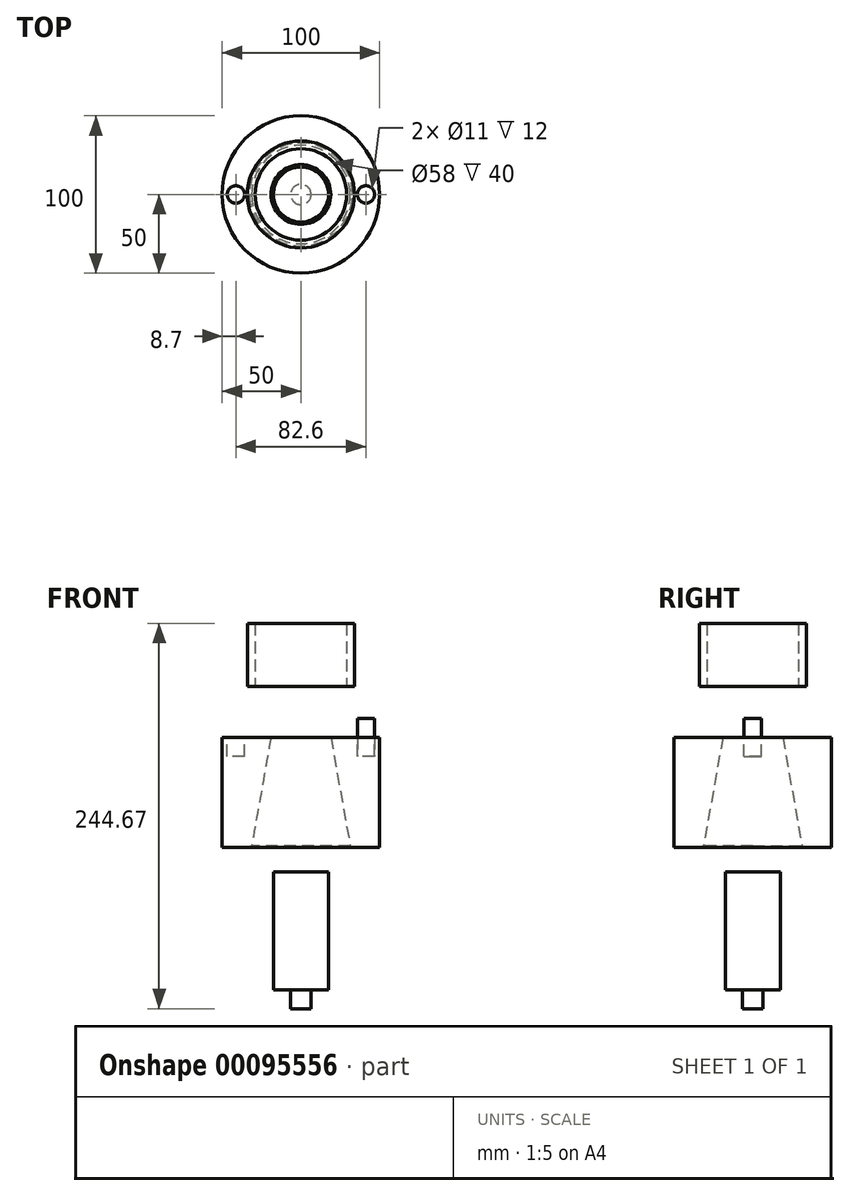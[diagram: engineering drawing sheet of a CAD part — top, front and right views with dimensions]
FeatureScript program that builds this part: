
annotation { "Feature Type Name" : "Feature", "Feature Type Description" : "" }
export const myFeature = defineFeature(function(context is Context, id is Id, definition is map)
    precondition{}
    {
        {
            var Q0;
            Q0=qCreatedBy(makeId("Front.planeOp"),FACE);
            var sketch = newSketch(context, id + "F0", { "sketchPlane" : qUnion([Q0])});
            skLineSegment(sketch, "E0.bottom", {"start": v(50, 35) * mm, "end": v(-50, 35) * mm});
            skLineSegment(sketch, "E0.top", {"start": v(50, -35) * mm, "end": v(-50, -35) * mm});
            skLineSegment(sketch, "E0.left", {"start": v(50, 35) * mm, "end": v(50, -35) * mm});
            skLineSegment(sketch, "E0.right", {"start": v(-50, 35) * mm, "end": v(-50, -35) * mm});
            skPoint(sketch, "E0.middle", {"position": v(0, 0) * mm});
            skLineSegment(sketch, "E1", {"start": v(-19, 35) * mm, "end": v(-31.5, -35) * mm});
            skLineSegment(sketch, "E2.MirrorCS", {"start": v(19, 35) * mm, "end": v(31.5, -35) * mm});
            skLineSegment(sketch, "E3.bottom", {"start": v(34, 107.38) * mm, "end": v(-34, 107.38) * mm});
            skLineSegment(sketch, "E3.top", {"start": v(34, 67.38) * mm, "end": v(-34, 67.38) * mm});
            skLineSegment(sketch, "E3.left", {"start": v(34, 107.38) * mm, "end": v(34, 67.38) * mm});
            skLineSegment(sketch, "E3.right", {"start": v(-34, 107.38) * mm, "end": v(-34, 67.38) * mm});
            skPoint(sketch, "E3.middle", {"position": v(0, 87.38) * mm});
            skLineSegment(sketch, "E4.bottom", {"start": v(29, 107.38) * mm, "end": v(-29, 107.38) * mm});
            skLineSegment(sketch, "E4.top", {"start": v(29, 67.38) * mm, "end": v(-29, 67.38) * mm});
            skLineSegment(sketch, "E4.left", {"start": v(29, 107.38) * mm, "end": v(29, 67.38) * mm});
            skLineSegment(sketch, "E4.right", {"start": v(-29, 107.38) * mm, "end": v(-29, 67.38) * mm});
            skLineSegment(sketch, "E5.bottom", {"start": v(17.5, -125.29) * mm, "end": v(-17.5, -125.29) * mm});
            skLineSegment(sketch, "E5.top", {"start": v(17.5, -50.29) * mm, "end": v(-17.5, -50.29) * mm});
            skLineSegment(sketch, "E5.left", {"start": v(17.5, -125.29) * mm, "end": v(17.5, -50.29) * mm});
            skLineSegment(sketch, "E5.right", {"start": v(-17.5, -125.29) * mm, "end": v(-17.5, -50.29) * mm});
            skPoint(sketch, "E5.middle", {"position": v(0, -87.79) * mm});
            skLineSegment(sketch, "E6.bottom", {"start": v(-6.5, -137.29) * mm, "end": v(6.5, -137.29) * mm});
            skLineSegment(sketch, "E6.left", {"start": v(-6.5, -137.29) * mm, "end": v(-6.5, -125.29) * mm});
            skLineSegment(sketch, "E6.right", {"start": v(6.5, -137.29) * mm, "end": v(6.5, -125.29) * mm});
            skPoint(sketch, "E6.middle", {"position": v(0, -125.29) * mm});
            skPoint(sketch, "E7", {"position": v(-6.5, -125.29) * mm});
            skPoint(sketch, "E8", {"position": v(6.5, -125.29) * mm});
            skLineSegment(sketch, "E9", {"start": v(0, -170.14) * mm, "end": v(0, 147.54) * mm});
            skPoint(sketch, "E9.endSnap0", {"position": v(0, 107.38) * mm});
            skPoint(sketch, "E10.middle", {"position": v(0, 35) * mm});
            skPoint(sketch, "E11", {"position": v(-41.3, 35) * mm});
            skPoint(sketch, "E12", {"position": v(41.3, 35) * mm});
            skLineSegment(sketch, "E13.bottom", {"start": v(-35.8, 47) * mm, "end": v(-46.8, 47) * mm});
            skLineSegment(sketch, "E13.top", {"start": v(-35.8, 23) * mm, "end": v(-46.8, 23) * mm});
            skLineSegment(sketch, "E13.left", {"start": v(-35.8, 47) * mm, "end": v(-35.8, 23) * mm});
            skLineSegment(sketch, "E13.right", {"start": v(-46.8, 47) * mm, "end": v(-46.8, 23) * mm});
            skLineSegment(sketch, "E14.MirrorCS", {"start": v(35.8, 23) * mm, "end": v(46.8, 23) * mm});
            skLineSegment(sketch, "E15.MirrorCS", {"start": v(35.8, 47) * mm, "end": v(35.8, 23) * mm});
            skLineSegment(sketch, "E16.MirrorCS", {"start": v(46.8, 47) * mm, "end": v(46.8, 23) * mm});
            skLineSegment(sketch, "E17.MirrorCS", {"start": v(35.8, 47) * mm, "end": v(46.8, 47) * mm});
            skLineSegment(sketch, "E18", {"start": v(-41.3, 23) * mm, "end": v(-41.3, 57) * mm});
            skLineSegment(sketch, "E19", {"start": v(41.3, 23) * mm, "end": v(41.3, 51.68) * mm});
            skPoint(sketch, "E19.endSnap0", {"position": v(41.3, 47) * mm});
            skSolve(sketch);
        }
        {
            var Q0;
            {var subQ0=sQuery(id+"F0.wireOp",EDGE,"E3.right");Q0=makeQuery(id+"F0.imprint","IMPRINT",FACE,{"disambiguationData":[TD([[makeQuery(id+"F0.imprint","IMPRINT",EDGE,{"derivedFrom":subQ0}),1.0]])]});}
            var Q1;
            Q1=sQuery(id+"F0.wireOp",EDGE,"E9");
            revolve(context, id + "F1", {"entities" : qUnion([Q0]), "axis" : qUnion([Q1]), "revolveType" : RevolveType.FULL});
        }
        {
            var Q0;
            {var subQ0=sQuery(id+"F0.wireOp",EDGE,"E0.right");Q0=makeQuery(id+"F0.imprint","IMPRINT",FACE,{"disambiguationData":[TD([[makeQuery(id+"F0.imprint","IMPRINT",EDGE,{"derivedFrom":subQ0}),1.0]])]});}
            var Q1;
            {var subQ5=sQuery(id+"F0.wireOp",EDGE,"E13.top");Q1=makeQuery(id+"F0.imprint","IMPRINT",FACE,{"disambiguationData":[TD([[makeQuery(id+"F0.imprint","IMPRINT",EDGE,{"derivedFrom":subQ5}),-1.0]])]});}
            var Q2;
            Q2=sQuery(id+"F0.wireOp",EDGE,"E9");
            revolve(context, id + "F2", {"entities" : qUnion([Q0, Q1]), "axis" : qUnion([Q2]), "revolveType" : RevolveType.FULL});
        }
        {
            var Q0;
            {var subQ0=sQuery(id+"F0.wireOp",EDGE,"E5.right");Q0=makeQuery(id+"F0.imprint","IMPRINT",FACE,{"disambiguationData":[TD([[makeQuery(id+"F0.imprint","IMPRINT",EDGE,{"derivedFrom":subQ0}),-1.0]])]});}
            var Q1;
            {var subQ0=sQuery(id+"F0.wireOp",EDGE,"E6.left");Q1=makeQuery(id+"F0.imprint","IMPRINT",FACE,{"disambiguationData":[TD([[makeQuery(id+"F0.imprint","IMPRINT",EDGE,{"derivedFrom":subQ0}),-1.0]])]});}
            var Q2;
            Q2=sQuery(id+"F0.wireOp",EDGE,"E9");
            revolve(context, id + "F3", {"entities" : qUnion([Q0, Q1]), "axis" : qUnion([Q2]), "revolveType" : RevolveType.FULL});
        }
        {
            var Q0;
            Q0=makeQuery(id+"F2.opRevolve","SWEPT_EDGE",EDGE,{"disambiguationData":[OSD([sQuery(id+"F0.wireOp",EDGE,"E0.top"),sQuery(id+"F0.wireOp",EDGE,"E1")])]});
            chamfer(context, id + "F4", {"entities" : qUnion([Q0]), "width" : 1.5 * mm});
        }
        {
            var Q0;
            {var subQ0=sQuery(id+"F0.wireOp",EDGE,"E13.right");var subQ1=sQuery(id+"F0.wireOp",EDGE,"E0.bottom");var subQ2=makeQuery(id+"F0.imprint","INTERSECT",VERTEX,{"derivedFrom":[subQ1,subQ0]});Q0=makeQuery(id+"F0.imprint","IMPRINT",FACE,{"disambiguationData":[TD([[makeQuery(id+"F0.imprint","IMPRINT",EDGE,{"disambiguationData":[TD([[subQ2,1.0]])],"derivedFrom":subQ1}),1.0]])]});}
            var Q1;
            {var subQ0=sQuery(id+"F0.wireOp",EDGE,"E13.right");var subQ1=sQuery(id+"F0.wireOp",EDGE,"E0.bottom");var subQ2=makeQuery(id+"F0.imprint","INTERSECT",VERTEX,{"derivedFrom":[subQ1,subQ0]});Q1=makeQuery(id+"F0.imprint","IMPRINT",FACE,{"disambiguationData":[TD([[makeQuery(id+"F0.imprint","IMPRINT",EDGE,{"disambiguationData":[TD([[subQ2,1.0]])],"derivedFrom":subQ1}),-1.0]])]});}
            var Q2;
            Q2=sQuery(id+"F0.wireOp",EDGE,"E18");
            revolve(context, id + "F5", {"operationType" : NewBodyOperationType.REMOVE, "entities" : qUnion([Q0, Q1]), "axis" : qUnion([Q2]), "revolveType" : RevolveType.FULL, "oppositeDirection" : true});
        }
        {
            var Q0;
            {var subQ0=sQuery(id+"F0.wireOp",EDGE,"E15.MirrorCS");var subQ1=sQuery(id+"F0.wireOp",EDGE,"E0.bottom");var subQ2=makeQuery(id+"F0.imprint","INTERSECT",VERTEX,{"derivedFrom":[subQ1,subQ0]});Q0=makeQuery(id+"F0.imprint","IMPRINT",FACE,{"disambiguationData":[TD([[makeQuery(id+"F0.imprint","IMPRINT",EDGE,{"disambiguationData":[TD([[subQ2,1.0]])],"derivedFrom":subQ1}),-1.0]])]});}
            var Q1;
            {var subQ0=sQuery(id+"F0.wireOp",EDGE,"E15.MirrorCS");var subQ1=sQuery(id+"F0.wireOp",EDGE,"E0.bottom");var subQ2=makeQuery(id+"F0.imprint","INTERSECT",VERTEX,{"derivedFrom":[subQ1,subQ0]});Q1=makeQuery(id+"F0.imprint","IMPRINT",FACE,{"disambiguationData":[TD([[makeQuery(id+"F0.imprint","IMPRINT",EDGE,{"disambiguationData":[TD([[subQ2,1.0]])],"derivedFrom":subQ1}),1.0]])]});}
            var Q2;
            Q2=sQuery(id+"F0.wireOp",EDGE,"E19");
            revolve(context, id + "F6", {"operationType" : NewBodyOperationType.REMOVE, "entities" : qUnion([Q0, Q1]), "axis" : qUnion([Q2]), "revolveType" : RevolveType.FULL, "oppositeDirection" : true});
        }
        {
            var Q0;
            {var subQ0=sQuery(id+"F0.wireOp",EDGE,"E15.MirrorCS");var subQ1=sQuery(id+"F0.wireOp",EDGE,"E0.bottom");var subQ2=makeQuery(id+"F0.imprint","INTERSECT",VERTEX,{"derivedFrom":[subQ1,subQ0]});Q0=makeQuery(id+"F0.imprint","IMPRINT",FACE,{"disambiguationData":[TD([[makeQuery(id+"F0.imprint","IMPRINT",EDGE,{"disambiguationData":[TD([[subQ2,1.0]])],"derivedFrom":subQ1}),-1.0]])]});}
            var Q1;
            {var subQ0=sQuery(id+"F0.wireOp",EDGE,"E15.MirrorCS");var subQ1=sQuery(id+"F0.wireOp",EDGE,"E0.bottom");var subQ2=makeQuery(id+"F0.imprint","INTERSECT",VERTEX,{"derivedFrom":[subQ1,subQ0]});Q1=makeQuery(id+"F0.imprint","IMPRINT",FACE,{"disambiguationData":[TD([[makeQuery(id+"F0.imprint","IMPRINT",EDGE,{"disambiguationData":[TD([[subQ2,1.0]])],"derivedFrom":subQ1}),1.0]])]});}
            var Q2;
            Q2=sQuery(id+"F0.wireOp",EDGE,"E19");
            revolve(context, id + "F7", {"entities" : qUnion([Q0, Q1]), "axis" : qUnion([Q2]), "revolveType" : RevolveType.FULL});
        }
    });
